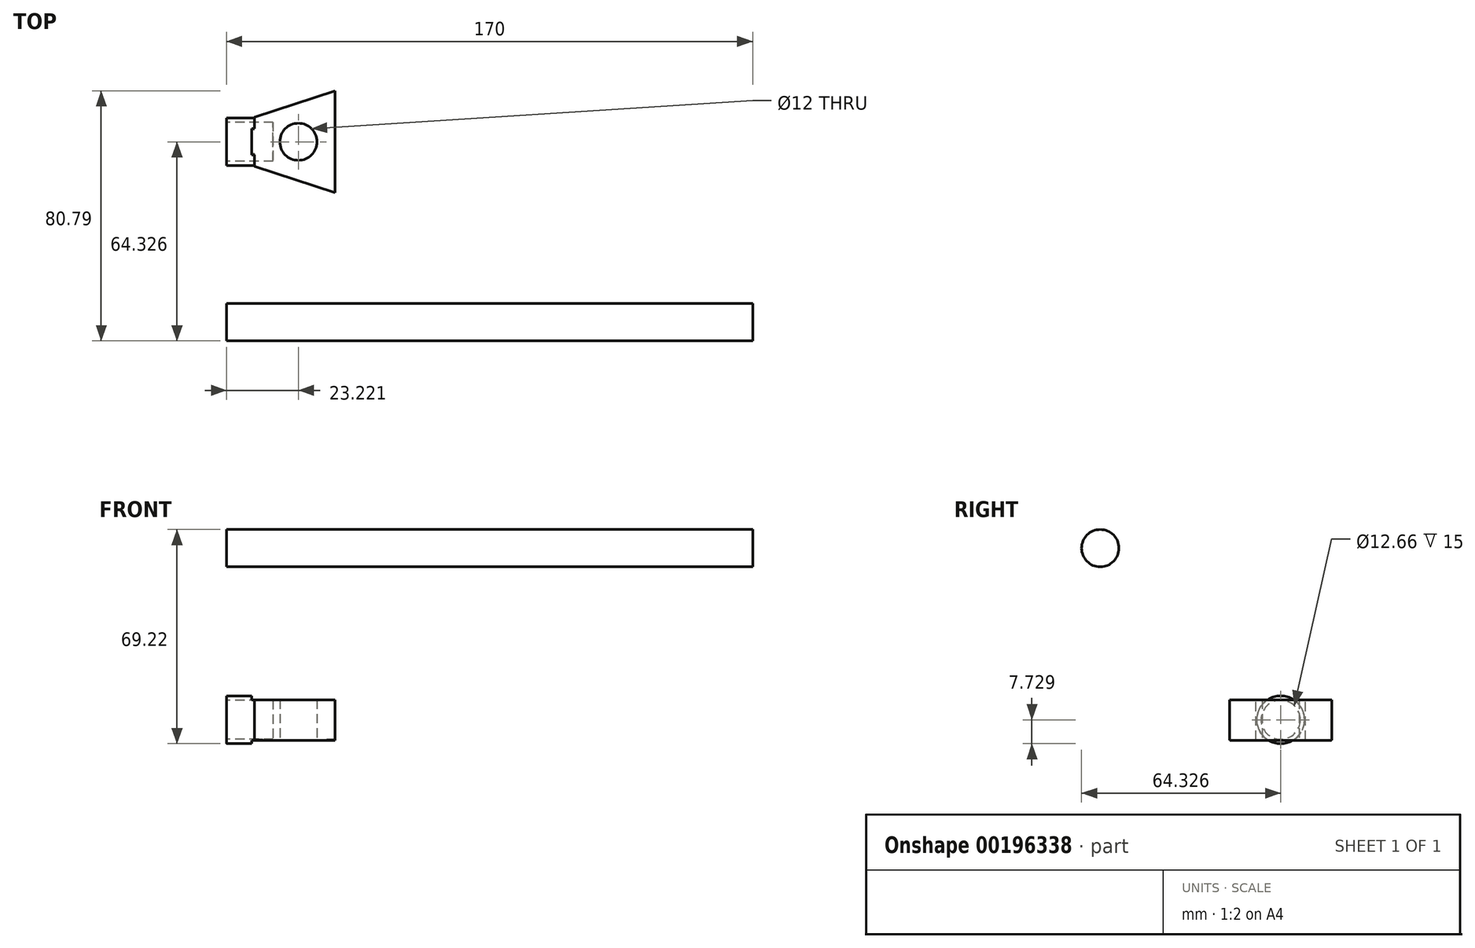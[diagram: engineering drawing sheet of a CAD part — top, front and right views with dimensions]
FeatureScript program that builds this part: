
annotation { "Feature Type Name" : "Feature", "Feature Type Description" : "" }
export const myFeature = defineFeature(function(context is Context, id is Id, definition is map)
    precondition{}
    {
        {
            var Q0;
            Q0=qCreatedBy(makeId("Right.planeOp"),FACE);
            var sketch = newSketch(context, id + "F0", { "sketchPlane" : qUnion([Q0])});
            skCircle(sketch, "E0", {"center": v(0, 0) * mm, "radius": 6.03 * mm});
            skSolve(sketch);
        }
        {
            var Q0;
            Q0=makeQuery(id+"F0.imprint","IMPRINT",FACE,{"disambiguationData":[TD([[makeQuery(id+"F0.imprint","IMPRINT",EDGE,{"derivedFrom":sQuery(id+"F0.wireOp",EDGE,"E0")}),1.0]])]});
            extrude(context, id + "F1", {"entities" : qUnion([Q0]), "depth" : 170 * mm});
        }
        {
            var Q0;
            Q0=qCreatedBy(makeId("Right.planeOp"),FACE);
            var sketch = newSketch(context, id + "F2", { "sketchPlane" : qUnion([Q0])});
            skCircle(sketch, "E1", {"center": v(58.3, -55.46) * mm, "radius": 7.73 * mm});
            skSolve(sketch);
        }
        {
            var Q0;
            Q0=qCreatedBy(makeId("Right.planeOp"),FACE);
            cPlane(context, id + "F3", {"entities" : qUnion([Q0]), "cplaneType" : CPlaneType.OFFSET, "offset" : 35 * mm, "width" : 150 * mm, "height" : 150 * mm});
        }
        {
            var Q0;
            Q0=qCreatedBy(id+"F3.planeOp",FACE);
            var sketch = newSketch(context, id + "F4", { "sketchPlane" : qUnion([Q0])});
            skCircle(sketch, "E2", {"center": v(58.3, -55.46) * mm, "radius": 17.7 * mm});
            skSolve(sketch);
        }
        {
            var Q0;
            Q0=makeQuery(id+"F4.imprint","IMPRINT",FACE,{"disambiguationData":[TD([[makeQuery(id+"F4.imprint","IMPRINT",EDGE,{"derivedFrom":sQuery(id+"F4.wireOp",EDGE,"E2")}),1.0]])]});
            var Q1;
            Q1=makeQuery(id+"F2.imprint","IMPRINT",FACE,{"disambiguationData":[TD([[makeQuery(id+"F2.imprint","IMPRINT",EDGE,{"derivedFrom":sQuery(id+"F2.wireOp",EDGE,"E1")}),1.0]])]});
            loft(context, id + "F5", {"sheetProfilesArray" : [{ "sheetProfileEntities" : qUnion([Q0]) }, { "sheetProfileEntities" : qUnion([Q1]) }]});
        }
        {
            var Q0;
            Q0=qCreatedBy(makeId("Front.planeOp"),FACE);
            var sketch = newSketch(context, id + "F6", { "sketchPlane" : qUnion([Q0])});
            skLineSegment(sketch, "E3", {"start": v(35.05, -62.15) * mm, "end": v(8.17, -62.15) * mm});
            skLineSegment(sketch, "E4", {"start": v(8.17, -48.98) * mm, "end": v(35.05, -48.98) * mm});
            skPoint(sketch, "E5.orphan", {"position": v(0, -48.98) * mm});
            skPoint(sketch, "E6.start.orphan", {"position": v(0, -47.9) * mm});
            skPoint(sketch, "E7.trimOffspring.end.orphan", {"position": v(0, -63.23) * mm});
            skPoint(sketch, "E8.end.orphan", {"position": v(0, -55.57) * mm});
            skPoint(sketch, "E8.start.orphan", {"position": v(0, -62.15) * mm});
            skLineSegment(sketch, "E9", {"start": v(8.17, -48.98) * mm, "end": v(8.17, -32.51) * mm});
            skLineSegment(sketch, "E10", {"start": v(8.17, -32.51) * mm, "end": v(35.05, -32.51) * mm});
            skLineSegment(sketch, "E11", {"start": v(35.05, -32.51) * mm, "end": v(35.05, -48.98) * mm});
            skLineSegment(sketch, "E12", {"start": v(8.17, -62.15) * mm, "end": v(8.17, -79.51) * mm});
            skLineSegment(sketch, "E13", {"start": v(8.17, -79.51) * mm, "end": v(35.05, -79.51) * mm});
            skLineSegment(sketch, "E14", {"start": v(35.05, -79.51) * mm, "end": v(35.05, -62.15) * mm});
            skSolve(sketch);
        }
        {
            var Q0;
            Q0 = qSketchRegion(id + "F6", true);
            extrude(context, id + "F7", {"entities" : qUnion([Q0]), "operationType" : NewBodyOperationType.REMOVE, "oppositeDirection" : true, "depth" : 100 * mm});
        }
        {
            var Q0;
            Q0=makeQuery(id+"F5.opLoft","CAP_FACE",FACE,{"disambiguationData":[OSD([makeQuery(id+"F2.imprint","IMPRINT",FACE,{"disambiguationData":[TD([[makeQuery(id+"F2.imprint","IMPRINT",EDGE,{"derivedFrom":sQuery(id+"F2.wireOp",EDGE,"E1")}),1.0]])]})])],"isStart":true});
            var sketch = newSketch(context, id + "F8", { "sketchPlane" : qUnion([Q0])});
            skCircle(sketch, "E15", {"center": v(-58.3, -55.46) * mm, "radius": 7.73 * mm});
            skCircle(sketch, "E16", {"center": v(-58.3, -55.46) * mm, "radius": 11.56 * mm});
            skSolve(sketch);
        }
        {
            var Q0;
            Q0=makeQuery(id+"F8.imprint","IMPRINT",FACE,{"disambiguationData":[TD([[makeQuery(id+"F8.imprint","IMPRINT",EDGE,{"derivedFrom":sQuery(id+"F8.wireOp",EDGE,"E15")}),-1.0]])]});
            extrude(context, id + "F9", {"entities" : qUnion([Q0]), "operationType" : NewBodyOperationType.REMOVE, "oppositeDirection" : true, "depth" : 9 * mm});
        }
        {
            var Q0;
            Q0=makeQuery(id+"F7.boolean.opBoolean","COPY",FACE,{"derivedFrom":makeQuery(id+"F7.opExtrude","SWEPT_FACE",FACE,{"disambiguationData":[OSD([sQuery(id+"F6.wireOp",EDGE,"E4")])]})});
            var sketch = newSketch(context, id + "F10", { "sketchPlane" : qUnion([Q0])});
            skLineSegment(sketch, "E17", {"start": v(9, 66.29) * mm, "end": v(35, 74.76) * mm});
            skLineSegment(sketch, "E18", {"start": v(35, 74.76) * mm, "end": v(35, 77.78) * mm});
            skLineSegment(sketch, "E19", {"start": v(35, 77.78) * mm, "end": v(9, 69.8) * mm});
            skLineSegment(sketch, "E20", {"start": v(9, 69.8) * mm, "end": v(9, 66.29) * mm});
            skLineSegment(sketch, "E21", {"start": v(9, 50.3) * mm, "end": v(35, 41.84) * mm});
            skLineSegment(sketch, "E22", {"start": v(35, 41.84) * mm, "end": v(35, 38.41) * mm});
            skLineSegment(sketch, "E23", {"start": v(35, 38.41) * mm, "end": v(9, 46.11) * mm});
            skLineSegment(sketch, "E24", {"start": v(9, 46.11) * mm, "end": v(9, 50.3) * mm});
            skSolve(sketch);
        }
        {
            var Q0;
            Q0 = qSketchRegion(id + "F10", true);
            extrude(context, id + "F11", {"entities" : qUnion([Q0]), "operationType" : NewBodyOperationType.REMOVE, "oppositeDirection" : true, "depth" : 25 * mm});
        }
        {
            var Q0;
            Q0=makeQuery(id+"F7.boolean.opBoolean","COPY",FACE,{"derivedFrom":makeQuery(id+"F7.opExtrude","SWEPT_FACE",FACE,{"disambiguationData":[OSD([sQuery(id+"F6.wireOp",EDGE,"E3")])]})});
            var sketch = newSketch(context, id + "F12", { "sketchPlane" : qUnion([Q0])});
            skCircle(sketch, "E25", {"center": v(23.22, -58.3) * mm, "radius": 6 * mm});
            skPoint(sketch, "E25.centerSnap0", {"position": v(8.17, -58.3) * mm});
            skSolve(sketch);
        }
        {
            var Q0;
            Q0 = qSketchRegion(id + "F12", true);
            extrude(context, id + "F13", {"entities" : qUnion([Q0]), "operationType" : NewBodyOperationType.REMOVE, "oppositeDirection" : true, "depth" : 25 * mm});
        }
        {
            var Q0;
            Q0=makeQuery(id+"F5.opLoft","CAP_FACE",FACE,{"disambiguationData":[OSD([makeQuery(id+"F2.imprint","IMPRINT",FACE,{"disambiguationData":[TD([[makeQuery(id+"F2.imprint","IMPRINT",EDGE,{"derivedFrom":sQuery(id+"F2.wireOp",EDGE,"E1")}),1.0]])]})])],"isStart":true});
            var sketch = newSketch(context, id + "F14", { "sketchPlane" : qUnion([Q0])});
            skCircle(sketch, "E26", {"center": v(-58.3, -55.46) * mm, "radius": 6.33 * mm});
            skSolve(sketch);
        }
        {
            var Q0;
            Q0 = qSketchRegion(id + "F14", true);
            extrude(context, id + "F15", {"entities" : qUnion([Q0]), "operationType" : NewBodyOperationType.REMOVE, "oppositeDirection" : true, "depth" : 15 * mm});
        }
    });
